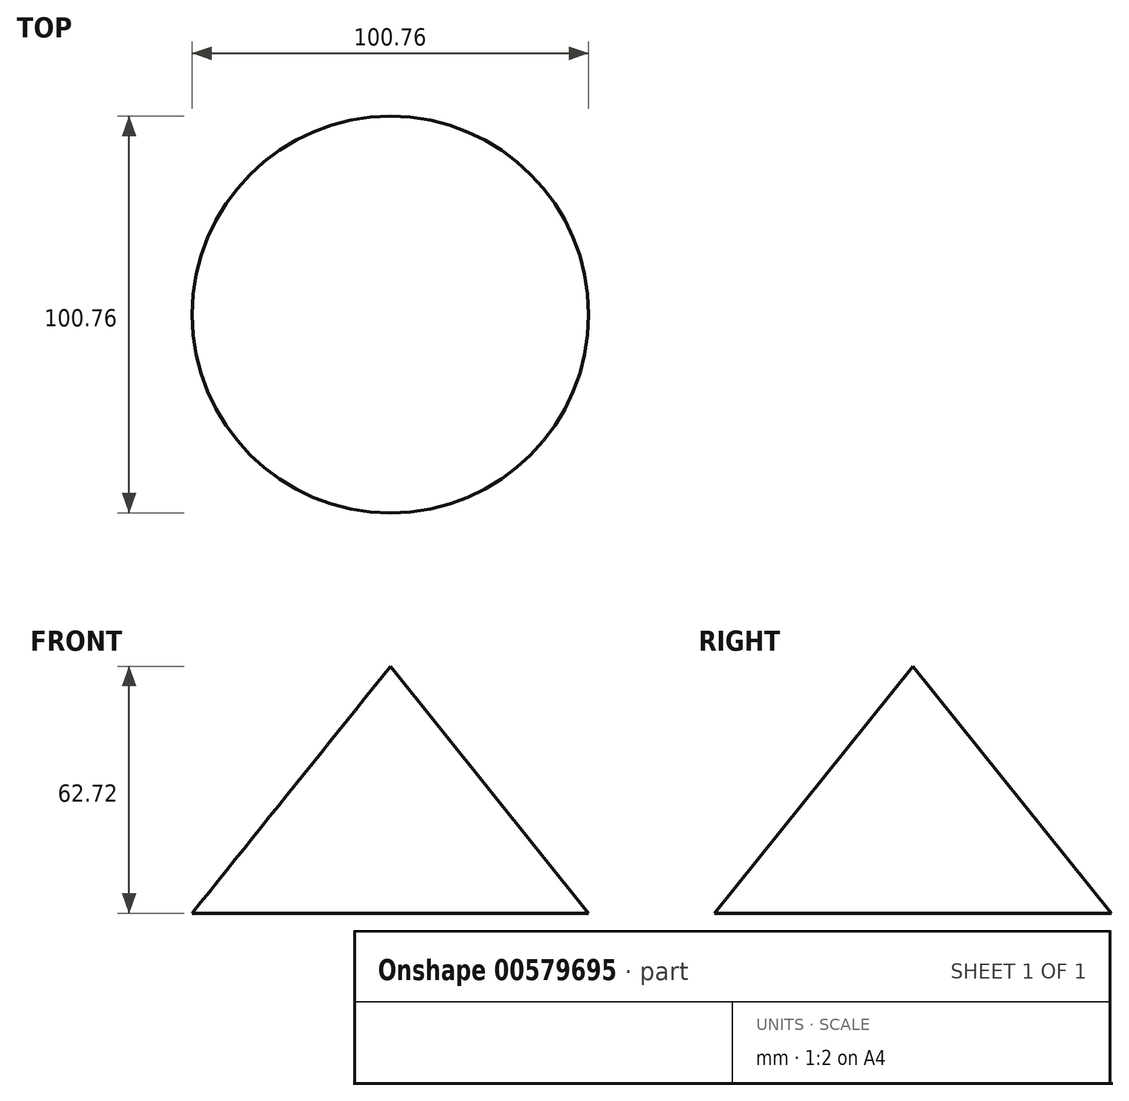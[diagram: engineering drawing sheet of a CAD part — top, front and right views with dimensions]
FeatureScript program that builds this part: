
annotation { "Feature Type Name" : "Feature", "Feature Type Description" : "" }
export const myFeature = defineFeature(function(context is Context, id is Id, definition is map)
    precondition{}
    {
        {
            var Q0;
            Q0=qCreatedBy(makeId("Front.planeOp"),FACE);
            var sketch = newSketch(context, id + "F0", { "sketchPlane" : qUnion([Q0])});
            skLineSegment(sketch, "E0", {"start": v(0, 0) * mm, "end": v(50.38, 0) * mm});
            skLineSegment(sketch, "E1", {"start": v(50.38, 0) * mm, "end": v(0, 62.72) * mm});
            skLineSegment(sketch, "E2", {"start": v(0, 62.72) * mm, "end": v(0, 0) * mm});
            skSolve(sketch);
        }
        {
            var Q0;
            Q0 = qSketchRegion(id + "F0", true);
            var Q1;
            Q1=sQuery(id+"F0.wireOp",EDGE,"E2");
            revolve(context, id + "F1", {"entities" : qUnion([Q0]), "axis" : qUnion([Q1]), "revolveType" : RevolveType.FULL});
        }
    });
